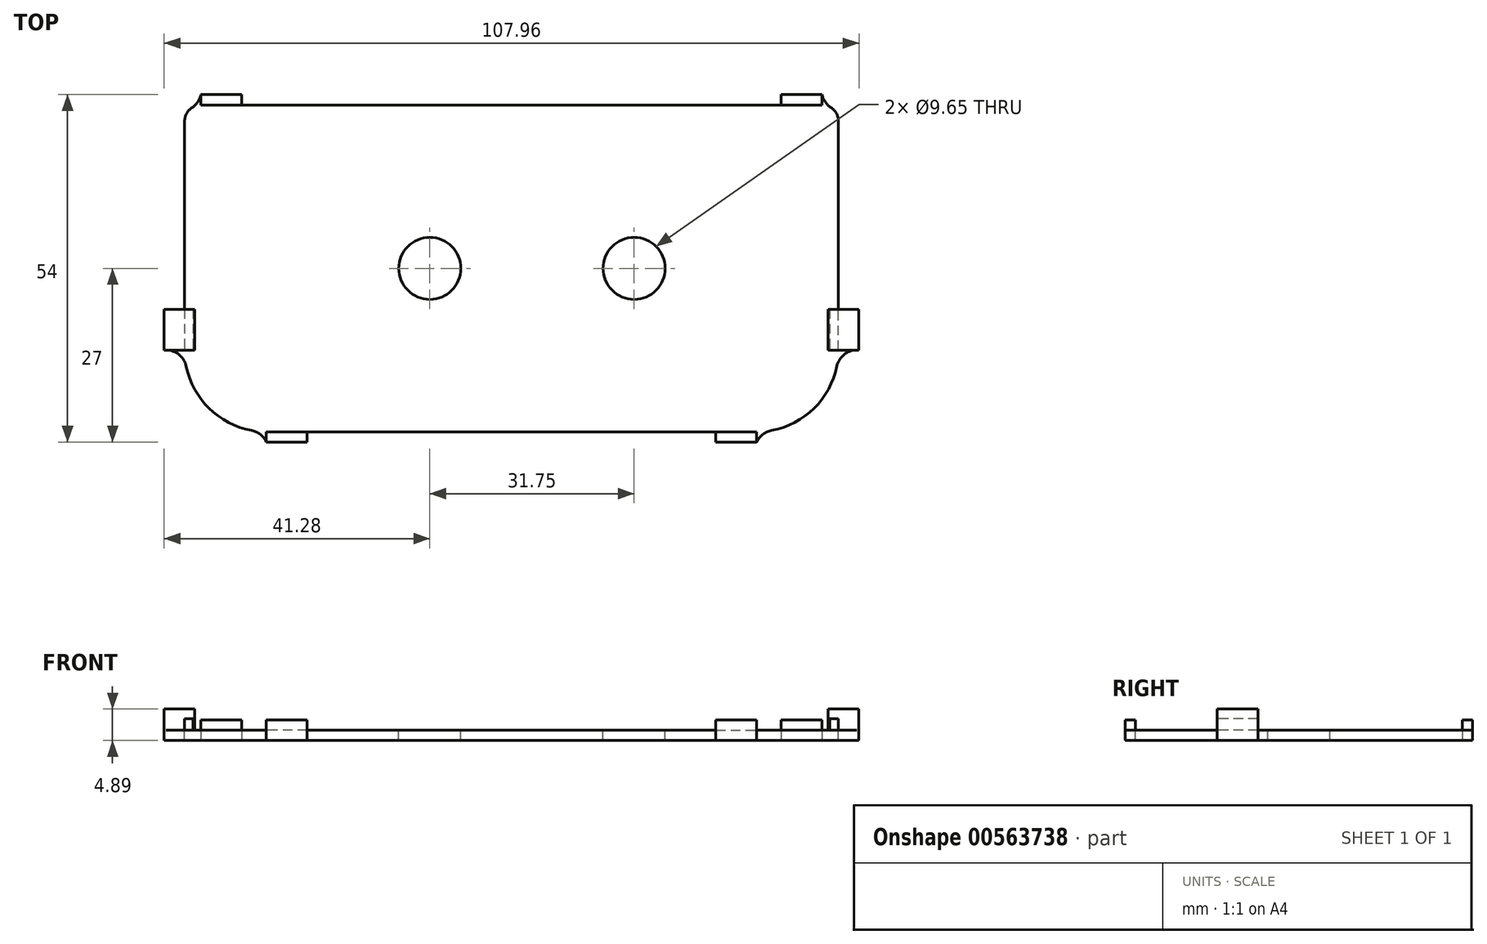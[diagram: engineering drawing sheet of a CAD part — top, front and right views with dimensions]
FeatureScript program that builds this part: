
annotation { "Feature Type Name" : "Feature", "Feature Type Description" : "" }
export const myFeature = defineFeature(function(context is Context, id is Id, definition is map)
    precondition{}
    {
        {
            var Q0;
            Q0=qCreatedBy(makeId("Top.planeOp"),FACE);
            var sketch = newSketch(context, id + "F0", { "sketchPlane" : qUnion([Q0])});
            skLineSegment(sketch, "E0.bottom", {"start": v(50.8, 25.4) * mm, "end": v(-50.8, 25.4) * mm});
            skLineSegment(sketch, "E0.top", {"start": v(50.8, -25.4) * mm, "end": v(-50.8, -25.4) * mm});
            skLineSegment(sketch, "E0.left", {"start": v(50.8, 25.4) * mm, "end": v(50.8, -25.4) * mm});
            skLineSegment(sketch, "E0.right", {"start": v(-50.8, 25.4) * mm, "end": v(-50.8, -25.4) * mm});
            skPoint(sketch, "E0.middle", {"position": v(0, 0) * mm});
            skLineSegment(sketch, "E1", {"start": v(-50.8, 0) * mm, "end": v(50.8, 0) * mm, "construction": true});
            skCircle(sketch, "E2", {"center": v(19.05, 0) * mm, "radius": 1.9 * mm});
            skCircle(sketch, "E3", {"center": v(-12.7, 0) * mm, "radius": 1.9 * mm});
            skSolve(sketch);
        }
        {
            var Q0;
            Q0=makeQuery(id+"F0.imprint","IMPRINT",FACE,{"disambiguationData":[TD([[makeQuery(id+"F0.imprint","IMPRINT",EDGE,{"derivedFrom":sQuery(id+"F0.wireOp",EDGE,"E0.bottom")}),1.0]])]});
            extrude(context, id + "F1", {"entities" : qUnion([Q0]), "depth" : 1.59 * mm, "offsetDistance" : 25.4 * mm});
        }
        {
            var Q0;
            Q0=makeQuery(id+"F1.opExtrude","CAP_FACE",FACE,{"disambiguationData":[OSD([sQuery(id+"F0.wireOp",EDGE,"E0.bottom"),sQuery(id+"F0.wireOp",EDGE,"E0.top"),sQuery(id+"F0.wireOp",EDGE,"E0.left"),sQuery(id+"F0.wireOp",EDGE,"E0.right"),sQuery(id+"F0.wireOp",EDGE,"E2"),sQuery(id+"F0.wireOp",EDGE,"E3")])],"isStart":false});
            var sketch = newSketch(context, id + "F2", { "sketchPlane" : qUnion([Q0])});
            skCircle(sketch, "E4", {"center": v(-12.7, 10.8) * mm, "radius": 3.18 * mm});
            skCircle(sketch, "E5", {"center": v(19.05, 10.8) * mm, "radius": 3.18 * mm});
            skLineSegment(sketch, "E6", {"start": v(-12.7, 10.8) * mm, "end": v(-12.7, -25.4) * mm, "construction": true});
            skLineSegment(sketch, "E7", {"start": v(19.05, 10.8) * mm, "end": v(19.05, -25.4) * mm, "construction": true});
            skCircle(sketch, "E8", {"center": v(19.05, -10.8) * mm, "radius": 3.18 * mm});
            skCircle(sketch, "E9", {"center": v(-12.7, -10.8) * mm, "radius": 3.18 * mm});
            skCircle(sketch, "E10", {"center": v(19.05, 0) * mm, "radius": 4.83 * mm});
            skCircle(sketch, "E11", {"center": v(-12.7, 0) * mm, "radius": 4.83 * mm});
            skSolve(sketch);
        }
        {
            var Q0;
            Q0=makeQuery(id+"F1.opExtrude","SWEPT_EDGE",EDGE,{"disambiguationData":[OSD([sQuery(id+"F0.wireOp",EDGE,"E0.top"),sQuery(id+"F0.wireOp",EDGE,"E0.right")])]});
            var Q1;
            Q1=makeQuery(id+"F1.opExtrude","SWEPT_EDGE",EDGE,{"disambiguationData":[OSD([sQuery(id+"F0.wireOp",EDGE,"E0.top"),sQuery(id+"F0.wireOp",EDGE,"E0.left")])]});
            fillet(context, id + "F3", {"entities" : qUnion([Q0, Q1]), "radius" : 12.7 * mm, "tangentPropagation" : true, "allowEdgeOverflow" : false});
        }
        {
            var Q0;
            Q0=makeQuery(id+"F1.opExtrude","SWEPT_EDGE",EDGE,{"disambiguationData":[OSD([sQuery(id+"F0.wireOp",EDGE,"E0.bottom"),sQuery(id+"F0.wireOp",EDGE,"E0.right")])]});
            var Q1;
            Q1=makeQuery(id+"F1.opExtrude","SWEPT_EDGE",EDGE,{"disambiguationData":[OSD([sQuery(id+"F0.wireOp",EDGE,"E0.bottom"),sQuery(id+"F0.wireOp",EDGE,"E0.left")])]});
            fillet(context, id + "F4", {"entities" : qUnion([Q0, Q1]), "radius" : 2.54 * mm, "tangentPropagation" : true, "allowEdgeOverflow" : false});
        }
        {
            var Q0;
            Q0=makeQuery(id+"F2.imprint","IMPRINT",FACE,{"disambiguationData":[TD([[makeQuery(id+"F2.imprint","IMPRINT",EDGE,{"derivedFrom":sQuery(id+"F2.wireOp",EDGE,"E11")}),1.0]])]});
            var Q1;
            Q1=makeQuery(id+"F2.imprint","IMPRINT",FACE,{"disambiguationData":[TD([[makeQuery(id+"F2.imprint","IMPRINT",EDGE,{"derivedFrom":sQuery(id+"F2.wireOp",EDGE,"E10")}),1.0]])]});
            extrude(context, id + "F5", {"entities" : qUnion([Q0, Q1]), "operationType" : NewBodyOperationType.REMOVE, "oppositeDirection" : true, "depth" : 3.17 * mm, "offsetDistance" : 25.4 * mm});
        }
        {
            var Q0;
            Q0=makeQuery(id+"F1.opExtrude","SWEPT_FACE",FACE,{"disambiguationData":[OSD([sQuery(id+"F0.wireOp",EDGE,"E0.bottom")])]});
            var sketch = newSketch(context, id + "F6", { "sketchPlane" : qUnion([Q0])});
            skLineSegment(sketch, "E12.bottom", {"start": v(-48.26, 1.59) * mm, "end": v(-41.91, 1.59) * mm});
            skLineSegment(sketch, "E12.top", {"start": v(-48.26, 0) * mm, "end": v(-41.91, 0) * mm});
            skLineSegment(sketch, "E12.left", {"start": v(-48.26, 1.59) * mm, "end": v(-48.26, 0) * mm});
            skLineSegment(sketch, "E12.right", {"start": v(-41.91, 1.59) * mm, "end": v(-41.91, 0) * mm});
            skLineSegment(sketch, "E13.bottom", {"start": v(48.26, 1.59) * mm, "end": v(41.91, 1.59) * mm});
            skLineSegment(sketch, "E13.top", {"start": v(48.26, 0) * mm, "end": v(41.91, 0) * mm});
            skLineSegment(sketch, "E13.left", {"start": v(48.26, 1.59) * mm, "end": v(48.26, 0) * mm});
            skLineSegment(sketch, "E13.right", {"start": v(41.91, 1.59) * mm, "end": v(41.91, 0) * mm});
            skSolve(sketch);
        }
        {
            var Q0;
            Q0=makeQuery(id+"F6.imprint","IMPRINT",FACE,{"disambiguationData":[TD([[makeQuery(id+"F6.imprint","IMPRINT",EDGE,{"derivedFrom":sQuery(id+"F6.wireOp",EDGE,"E12.bottom")}),-1.0]])]});
            var Q1;
            Q1=makeQuery(id+"F6.imprint","IMPRINT",FACE,{"disambiguationData":[TD([[makeQuery(id+"F6.imprint","IMPRINT",EDGE,{"derivedFrom":sQuery(id+"F6.wireOp",EDGE,"E13.bottom")}),-1.0]])]});
            extrude(context, id + "F7", {"entities" : qUnion([Q0, Q1]), "operationType" : NewBodyOperationType.ADD, "depth" : 1.6 * mm, "offsetDistance" : 25.4 * mm});
        }
        {
            var Q0;
            Q0=makeQuery(id+"F1.opExtrude","SWEPT_FACE",FACE,{"disambiguationData":[OSD([sQuery(id+"F0.wireOp",EDGE,"E0.top")])]});
            var sketch = newSketch(context, id + "F8", { "sketchPlane" : qUnion([Q0])});
            skLineSegment(sketch, "E14.bottom", {"start": v(-38.1, 0) * mm, "end": v(-31.75, 0) * mm});
            skLineSegment(sketch, "E14.top", {"start": v(-38.1, 1.59) * mm, "end": v(-31.75, 1.59) * mm});
            skLineSegment(sketch, "E14.left", {"start": v(-38.1, 0) * mm, "end": v(-38.1, 1.59) * mm});
            skLineSegment(sketch, "E14.right", {"start": v(-31.75, 0) * mm, "end": v(-31.75, 1.59) * mm});
            skLineSegment(sketch, "E15.bottom", {"start": v(38.1, 0) * mm, "end": v(31.75, 0) * mm});
            skLineSegment(sketch, "E15.top", {"start": v(38.1, 1.59) * mm, "end": v(31.75, 1.59) * mm});
            skLineSegment(sketch, "E15.left", {"start": v(38.1, 0) * mm, "end": v(38.1, 1.59) * mm});
            skLineSegment(sketch, "E15.right", {"start": v(31.75, 0) * mm, "end": v(31.75, 1.59) * mm});
            skSolve(sketch);
        }
        {
            var Q0;
            Q0=makeQuery(id+"F8.imprint","IMPRINT",FACE,{"disambiguationData":[TD([[makeQuery(id+"F8.imprint","IMPRINT",EDGE,{"derivedFrom":sQuery(id+"F8.wireOp",EDGE,"E15.bottom")}),-1.0]])]});
            var Q1;
            Q1=makeQuery(id+"F8.imprint","IMPRINT",FACE,{"disambiguationData":[TD([[makeQuery(id+"F8.imprint","IMPRINT",EDGE,{"derivedFrom":sQuery(id+"F8.wireOp",EDGE,"E14.bottom")}),-1.0]])]});
            extrude(context, id + "F9", {"entities" : qUnion([Q0, Q1]), "operationType" : NewBodyOperationType.ADD, "depth" : 1.6 * mm, "offsetDistance" : 25.4 * mm});
        }
        {
            var Q0;
            Q0=makeQuery(id+"F1.opExtrude","SWEPT_FACE",FACE,{"disambiguationData":[OSD([sQuery(id+"F0.wireOp",EDGE,"E0.right")])]});
            var sketch = newSketch(context, id + "F10", { "sketchPlane" : qUnion([Q0])});
            skLineSegment(sketch, "E16.bottom", {"start": v(12.7, 0) * mm, "end": v(6.35, 0) * mm});
            skLineSegment(sketch, "E16.top", {"start": v(12.7, 1.59) * mm, "end": v(6.35, 1.59) * mm});
            skLineSegment(sketch, "E16.left", {"start": v(12.7, 0) * mm, "end": v(12.7, 1.59) * mm});
            skLineSegment(sketch, "E16.right", {"start": v(6.35, 0) * mm, "end": v(6.35, 1.59) * mm});
            skSolve(sketch);
        }
        {
            var Q0;
            Q0=makeQuery(id+"F10.imprint","IMPRINT",FACE,{"disambiguationData":[TD([[makeQuery(id+"F10.imprint","IMPRINT",EDGE,{"derivedFrom":sQuery(id+"F10.wireOp",EDGE,"E16.bottom")}),1.0]])]});
            extrude(context, id + "F11", {"entities" : qUnion([Q0]), "operationType" : NewBodyOperationType.ADD, "depth" : 3.17 * mm, "offsetDistance" : 25.4 * mm});
        }
        {
            var Q0;
            Q0=makeQuery(id+"F1.opExtrude","SWEPT_FACE",FACE,{"disambiguationData":[OSD([sQuery(id+"F0.wireOp",EDGE,"E0.left")])]});
            var sketch = newSketch(context, id + "F12", { "sketchPlane" : qUnion([Q0])});
            skLineSegment(sketch, "E17.bottom", {"start": v(-12.7, 0) * mm, "end": v(-6.35, 0) * mm});
            skLineSegment(sketch, "E17.top", {"start": v(-12.7, 1.59) * mm, "end": v(-6.35, 1.59) * mm});
            skLineSegment(sketch, "E17.left", {"start": v(-12.7, 0) * mm, "end": v(-12.7, 1.59) * mm});
            skLineSegment(sketch, "E17.right", {"start": v(-6.35, 0) * mm, "end": v(-6.35, 1.59) * mm});
            skSolve(sketch);
        }
        {
            var Q0;
            Q0=makeQuery(id+"F12.imprint","IMPRINT",FACE,{"disambiguationData":[TD([[makeQuery(id+"F12.imprint","IMPRINT",EDGE,{"derivedFrom":sQuery(id+"F12.wireOp",EDGE,"E17.bottom")}),-1.0]])]});
            extrude(context, id + "F13", {"entities" : qUnion([Q0]), "operationType" : NewBodyOperationType.ADD, "depth" : 3.17 * mm, "offsetDistance" : 25.4 * mm});
        }
        {
            var Q0;
            Q0=makeQuery(id+"F13.boolean.opBoolean","MERGE",FACE,{"derivedFrom":[makeQuery(id+"F11.boolean.opBoolean","MERGE",FACE,{"derivedFrom":[makeQuery(id+"F9.boolean.opBoolean","MERGE",FACE,{"derivedFrom":[makeQuery(id+"F7.boolean.opBoolean","MERGE",FACE,{"derivedFrom":[makeQuery(id+"F1.opExtrude","CAP_FACE",FACE,{"disambiguationData":[OSD([sQuery(id+"F0.wireOp",EDGE,"E0.bottom"),sQuery(id+"F0.wireOp",EDGE,"E0.top"),sQuery(id+"F0.wireOp",EDGE,"E0.left"),sQuery(id+"F0.wireOp",EDGE,"E0.right"),sQuery(id+"F0.wireOp",EDGE,"E2"),sQuery(id+"F0.wireOp",EDGE,"E3")])],"isStart":false}),makeQuery(id+"F7.opExtrude","SWEPT_FACE",FACE,{"disambiguationData":[OSD([sQuery(id+"F6.wireOp",EDGE,"E12.bottom")])]}),makeQuery(id+"F7.opExtrude","SWEPT_FACE",FACE,{"disambiguationData":[OSD([sQuery(id+"F6.wireOp",EDGE,"E13.bottom")])]})]}),makeQuery(id+"F9.opExtrude","SWEPT_FACE",FACE,{"disambiguationData":[OSD([sQuery(id+"F8.wireOp",EDGE,"E14.top")])]}),makeQuery(id+"F9.opExtrude","SWEPT_FACE",FACE,{"disambiguationData":[OSD([sQuery(id+"F8.wireOp",EDGE,"E15.top")])]})]}),makeQuery(id+"F11.opExtrude","SWEPT_FACE",FACE,{"disambiguationData":[OSD([sQuery(id+"F10.wireOp",EDGE,"E16.top")])]})]}),makeQuery(id+"F13.opExtrude","SWEPT_FACE",FACE,{"disambiguationData":[OSD([sQuery(id+"F12.wireOp",EDGE,"E17.top")])]})]});
            var sketch = newSketch(context, id + "F14", { "sketchPlane" : qUnion([Q0])});
            skLineSegment(sketch, "E18.bottom", {"start": v(31.75, -27) * mm, "end": v(38.1, -27) * mm});
            skLineSegment(sketch, "E18.top", {"start": v(31.75, -25.4) * mm, "end": v(38.1, -25.4) * mm});
            skLineSegment(sketch, "E18.left", {"start": v(31.75, -27) * mm, "end": v(31.75, -25.4) * mm});
            skLineSegment(sketch, "E18.right", {"start": v(38.1, -27) * mm, "end": v(38.1, -25.4) * mm});
            skLineSegment(sketch, "E19.bottom", {"start": v(53.98, -12.7) * mm, "end": v(50.8, -12.7) * mm});
            skLineSegment(sketch, "E19.top", {"start": v(53.98, -6.35) * mm, "end": v(50.8, -6.35) * mm});
            skLineSegment(sketch, "E19.left", {"start": v(53.98, -12.7) * mm, "end": v(53.98, -6.35) * mm});
            skLineSegment(sketch, "E19.right", {"start": v(50.8, -12.7) * mm, "end": v(50.8, -6.35) * mm});
            skLineSegment(sketch, "E20.bottom", {"start": v(48.26, 27) * mm, "end": v(41.91, 27) * mm});
            skLineSegment(sketch, "E20.top", {"start": v(48.26, 25.4) * mm, "end": v(41.91, 25.4) * mm});
            skLineSegment(sketch, "E20.left", {"start": v(48.26, 27) * mm, "end": v(48.26, 25.4) * mm});
            skLineSegment(sketch, "E20.right", {"start": v(41.91, 27) * mm, "end": v(41.91, 25.4) * mm});
            skLineSegment(sketch, "E21.bottom", {"start": v(-41.91, 27) * mm, "end": v(-48.26, 27) * mm});
            skLineSegment(sketch, "E21.top", {"start": v(-41.91, 25.4) * mm, "end": v(-48.26, 25.4) * mm});
            skLineSegment(sketch, "E21.left", {"start": v(-41.91, 27) * mm, "end": v(-41.91, 25.4) * mm});
            skLineSegment(sketch, "E21.right", {"start": v(-48.26, 27) * mm, "end": v(-48.26, 25.4) * mm});
            skLineSegment(sketch, "E22.bottom", {"start": v(-53.98, -12.7) * mm, "end": v(-50.8, -12.7) * mm});
            skLineSegment(sketch, "E22.top", {"start": v(-53.98, -6.35) * mm, "end": v(-50.8, -6.35) * mm});
            skLineSegment(sketch, "E22.left", {"start": v(-53.98, -12.7) * mm, "end": v(-53.98, -6.35) * mm});
            skLineSegment(sketch, "E22.right", {"start": v(-50.8, -12.7) * mm, "end": v(-50.8, -6.35) * mm});
            skLineSegment(sketch, "E23.bottom", {"start": v(-31.75, -25.4) * mm, "end": v(-38.1, -25.4) * mm});
            skLineSegment(sketch, "E23.top", {"start": v(-31.75, -27) * mm, "end": v(-38.1, -27) * mm});
            skLineSegment(sketch, "E23.left", {"start": v(-31.75, -25.4) * mm, "end": v(-31.75, -27) * mm});
            skLineSegment(sketch, "E23.right", {"start": v(-38.1, -25.4) * mm, "end": v(-38.1, -27) * mm});
            skSolve(sketch);
        }
        {
            var Q0;
            Q0=makeQuery(id+"F14.imprint","IMPRINT",FACE,{"disambiguationData":[TD([[makeQuery(id+"F14.imprint","IMPRINT",EDGE,{"derivedFrom":sQuery(id+"F14.wireOp",EDGE,"E20.bottom")}),1.0]])]});
            var Q1;
            Q1=makeQuery(id+"F14.imprint","IMPRINT",FACE,{"disambiguationData":[TD([[makeQuery(id+"F14.imprint","IMPRINT",EDGE,{"derivedFrom":sQuery(id+"F14.wireOp",EDGE,"E18.bottom")}),-1.0]])]});
            var Q2;
            Q2=makeQuery(id+"F14.imprint","IMPRINT",FACE,{"disambiguationData":[TD([[makeQuery(id+"F14.imprint","IMPRINT",EDGE,{"derivedFrom":sQuery(id+"F14.wireOp",EDGE,"E23.bottom")}),1.0]])]});
            var Q3;
            Q3=makeQuery(id+"F14.imprint","IMPRINT",FACE,{"disambiguationData":[TD([[makeQuery(id+"F14.imprint","IMPRINT",EDGE,{"derivedFrom":sQuery(id+"F14.wireOp",EDGE,"E21.bottom")}),1.0]])]});
            extrude(context, id + "F15", {"entities" : qUnion([Q0, Q1, Q2, Q3]), "operationType" : NewBodyOperationType.ADD, "depth" : 1.59 * mm, "offsetDistance" : 25.4 * mm});
        }
        {
            var Q0;
            Q0=makeQuery(id+"F14.imprint","IMPRINT",FACE,{"disambiguationData":[TD([[makeQuery(id+"F14.imprint","IMPRINT",EDGE,{"derivedFrom":sQuery(id+"F14.wireOp",EDGE,"E19.bottom")}),-1.0]])]});
            var Q1;
            Q1=makeQuery(id+"F14.imprint","IMPRINT",FACE,{"disambiguationData":[TD([[makeQuery(id+"F14.imprint","IMPRINT",EDGE,{"derivedFrom":sQuery(id+"F14.wireOp",EDGE,"E22.bottom")}),1.0]])]});
            extrude(context, id + "F16", {"entities" : qUnion([Q0, Q1]), "operationType" : NewBodyOperationType.ADD, "depth" : 3.3 * mm, "offsetDistance" : 25.4 * mm});
        }
        {
            var Q0;
            Q0=makeQuery(id+"F16.opExtrude","SWEPT_FACE",FACE,{"disambiguationData":[OSD([sQuery(id+"F14.wireOp",EDGE,"E22.right")])]});
            var sketch = newSketch(context, id + "F17", { "sketchPlane" : qUnion([Q0])});
            skLineSegment(sketch, "E24.bottom", {"start": v(-6.35, 4.89) * mm, "end": v(-12.7, 4.89) * mm});
            skLineSegment(sketch, "E24.top", {"start": v(-6.35, 3.37) * mm, "end": v(-12.7, 3.37) * mm});
            skLineSegment(sketch, "E24.left", {"start": v(-6.35, 4.89) * mm, "end": v(-6.35, 3.37) * mm});
            skLineSegment(sketch, "E24.right", {"start": v(-12.7, 4.89) * mm, "end": v(-12.7, 3.37) * mm});
            skSolve(sketch);
        }
        {
            var Q0;
            Q0=makeQuery(id+"F17.imprint","IMPRINT",FACE,{"disambiguationData":[TD([[makeQuery(id+"F17.imprint","IMPRINT",EDGE,{"derivedFrom":sQuery(id+"F17.wireOp",EDGE,"E24.bottom")}),-1.0]])]});
            extrude(context, id + "F18", {"entities" : qUnion([Q0]), "operationType" : NewBodyOperationType.ADD, "depth" : 1.59 * mm, "offsetDistance" : 25.4 * mm});
        }
        {
            var Q0;
            Q0=makeQuery(id+"F16.opExtrude","SWEPT_FACE",FACE,{"disambiguationData":[OSD([sQuery(id+"F14.wireOp",EDGE,"E19.right")])]});
            var sketch = newSketch(context, id + "F19", { "sketchPlane" : qUnion([Q0])});
            skLineSegment(sketch, "E25.bottom", {"start": v(12.7, 4.89) * mm, "end": v(6.35, 4.89) * mm});
            skLineSegment(sketch, "E25.top", {"start": v(12.7, 3.37) * mm, "end": v(6.35, 3.37) * mm});
            skLineSegment(sketch, "E25.left", {"start": v(12.7, 4.89) * mm, "end": v(12.7, 3.37) * mm});
            skLineSegment(sketch, "E25.right", {"start": v(6.35, 4.89) * mm, "end": v(6.35, 3.37) * mm});
            skSolve(sketch);
        }
        {
            var Q0;
            Q0=makeQuery(id+"F19.imprint","IMPRINT",FACE,{"disambiguationData":[TD([[makeQuery(id+"F19.imprint","IMPRINT",EDGE,{"derivedFrom":sQuery(id+"F19.wireOp",EDGE,"E25.bottom")}),1.0]])]});
            extrude(context, id + "F20", {"entities" : qUnion([Q0]), "operationType" : NewBodyOperationType.ADD, "depth" : 1.59 * mm, "offsetDistance" : 25.4 * mm});
        }
        {
            var Q0;
            Q0=makeQuery(id+"F9.opExtrude","CAP_EDGE",EDGE,{"disambiguationData":[OSD([sQuery(id+"F8.wireOp",EDGE,"E14.right")])],"isStart":true});
            var Q1;
            {var subQ0=sQuery(id+"F0.wireOp",EDGE,"E0.top");Q1=makeQuery(id+"F9.boolean.opBoolean","MERGE",EDGE,{"derivedFrom":[makeQuery(id+"F3.opFillet","BLEND_EDGE",EDGE,{"blendedFrom":[makeQuery(id+"F1.opExtrude","SWEPT_EDGE",EDGE,{"disambiguationData":[OSD([subQ0,sQuery(id+"F0.wireOp",EDGE,"E0.right")])]}),makeQuery(id+"F1.opExtrude","SWEPT_FACE",FACE,{"disambiguationData":[OSD([subQ0])]})],"blendedInto":[makeQuery(id+"F1.opExtrude","SWEPT_FACE",FACE,{"disambiguationData":[OSD([subQ0])]})]}),makeQuery(id+"F9.opExtrude","CAP_EDGE",EDGE,{"disambiguationData":[OSD([sQuery(id+"F8.wireOp",EDGE,"E14.left")])],"isStart":true})]});}
            var Q2;
            {var subQ0=sQuery(id+"F0.wireOp",EDGE,"E0.right");Q2=makeQuery(id+"F11.boolean.opBoolean","MERGE",EDGE,{"derivedFrom":[makeQuery(id+"F3.opFillet","BLEND_EDGE",EDGE,{"blendedFrom":[makeQuery(id+"F1.opExtrude","SWEPT_EDGE",EDGE,{"disambiguationData":[OSD([sQuery(id+"F0.wireOp",EDGE,"E0.top"),subQ0])]}),makeQuery(id+"F1.opExtrude","SWEPT_FACE",FACE,{"disambiguationData":[OSD([subQ0])]})],"blendedInto":[makeQuery(id+"F1.opExtrude","SWEPT_FACE",FACE,{"disambiguationData":[OSD([subQ0])]})]}),makeQuery(id+"F11.opExtrude","CAP_EDGE",EDGE,{"disambiguationData":[OSD([sQuery(id+"F10.wireOp",EDGE,"E16.left")])],"isStart":true})]});}
            var Q3;
            Q3=makeQuery(id+"F11.opExtrude","CAP_EDGE",EDGE,{"disambiguationData":[OSD([sQuery(id+"F10.wireOp",EDGE,"E16.right")])],"isStart":true});
            var Q4;
            {var subQ0=sQuery(id+"F0.wireOp",EDGE,"E0.bottom");Q4=makeQuery(id+"F7.boolean.opBoolean","MERGE",EDGE,{"derivedFrom":[makeQuery(id+"F4.opFillet","BLEND_EDGE",EDGE,{"blendedFrom":[makeQuery(id+"F1.opExtrude","SWEPT_EDGE",EDGE,{"disambiguationData":[OSD([subQ0,sQuery(id+"F0.wireOp",EDGE,"E0.right")])]}),makeQuery(id+"F1.opExtrude","SWEPT_FACE",FACE,{"disambiguationData":[OSD([subQ0])]})],"blendedInto":[makeQuery(id+"F1.opExtrude","SWEPT_FACE",FACE,{"disambiguationData":[OSD([subQ0])]})]}),makeQuery(id+"F7.opExtrude","CAP_EDGE",EDGE,{"disambiguationData":[OSD([sQuery(id+"F6.wireOp",EDGE,"E13.left")])],"isStart":true})]});}
            var Q5;
            Q5=makeQuery(id+"F7.opExtrude","CAP_EDGE",EDGE,{"disambiguationData":[OSD([sQuery(id+"F6.wireOp",EDGE,"E13.right")])],"isStart":true});
            var Q6;
            {var subQ0=sQuery(id+"F0.wireOp",EDGE,"E0.bottom");Q6=makeQuery(id+"F7.boolean.opBoolean","MERGE",EDGE,{"derivedFrom":[makeQuery(id+"F4.opFillet","BLEND_EDGE",EDGE,{"blendedFrom":[makeQuery(id+"F1.opExtrude","SWEPT_EDGE",EDGE,{"disambiguationData":[OSD([subQ0,sQuery(id+"F0.wireOp",EDGE,"E0.left")])]}),makeQuery(id+"F1.opExtrude","SWEPT_FACE",FACE,{"disambiguationData":[OSD([subQ0])]})],"blendedInto":[makeQuery(id+"F1.opExtrude","SWEPT_FACE",FACE,{"disambiguationData":[OSD([subQ0])]})]}),makeQuery(id+"F7.opExtrude","CAP_EDGE",EDGE,{"disambiguationData":[OSD([sQuery(id+"F6.wireOp",EDGE,"E12.left")])],"isStart":true})]});}
            var Q7;
            Q7=makeQuery(id+"F7.opExtrude","CAP_EDGE",EDGE,{"disambiguationData":[OSD([sQuery(id+"F6.wireOp",EDGE,"E12.right")])],"isStart":true});
            var Q8;
            Q8=makeQuery(id+"F13.opExtrude","CAP_EDGE",EDGE,{"disambiguationData":[OSD([sQuery(id+"F12.wireOp",EDGE,"E17.right")])],"isStart":true});
            var Q9;
            {var subQ0=sQuery(id+"F0.wireOp",EDGE,"E0.left");Q9=makeQuery(id+"F13.boolean.opBoolean","MERGE",EDGE,{"derivedFrom":[makeQuery(id+"F3.opFillet","BLEND_EDGE",EDGE,{"blendedFrom":[makeQuery(id+"F1.opExtrude","SWEPT_EDGE",EDGE,{"disambiguationData":[OSD([sQuery(id+"F0.wireOp",EDGE,"E0.top"),subQ0])]}),makeQuery(id+"F1.opExtrude","SWEPT_FACE",FACE,{"disambiguationData":[OSD([subQ0])]})],"blendedInto":[makeQuery(id+"F1.opExtrude","SWEPT_FACE",FACE,{"disambiguationData":[OSD([subQ0])]})]}),makeQuery(id+"F13.opExtrude","CAP_EDGE",EDGE,{"disambiguationData":[OSD([sQuery(id+"F12.wireOp",EDGE,"E17.left")])],"isStart":true})]});}
            var Q10;
            {var subQ0=sQuery(id+"F0.wireOp",EDGE,"E0.top");Q10=makeQuery(id+"F9.boolean.opBoolean","MERGE",EDGE,{"derivedFrom":[makeQuery(id+"F3.opFillet","BLEND_EDGE",EDGE,{"blendedFrom":[makeQuery(id+"F1.opExtrude","SWEPT_EDGE",EDGE,{"disambiguationData":[OSD([subQ0,sQuery(id+"F0.wireOp",EDGE,"E0.left")])]}),makeQuery(id+"F1.opExtrude","SWEPT_FACE",FACE,{"disambiguationData":[OSD([subQ0])]})],"blendedInto":[makeQuery(id+"F1.opExtrude","SWEPT_FACE",FACE,{"disambiguationData":[OSD([subQ0])]})]}),makeQuery(id+"F9.opExtrude","CAP_EDGE",EDGE,{"disambiguationData":[OSD([sQuery(id+"F8.wireOp",EDGE,"E15.left")])],"isStart":true})]});}
            var Q11;
            Q11=makeQuery(id+"F9.opExtrude","CAP_EDGE",EDGE,{"disambiguationData":[OSD([sQuery(id+"F8.wireOp",EDGE,"E15.right")])],"isStart":true});
            fillet(context, id + "F21", {"entities" : qUnion([Q0, Q1, Q2, Q3, Q4, Q5, Q6, Q7, Q8, Q9, Q10, Q11]), "radius" : 3.17 * mm, "tangentPropagation" : true, "allowEdgeOverflow" : false});
        }
        {
            var Q0;
            Q0=makeQuery(id+"F20.opExtrude","SWEPT_FACE",FACE,{"disambiguationData":[OSD([sQuery(id+"F19.wireOp",EDGE,"E25.top")])]});
            var sketch = newSketch(context, id + "F22", { "sketchPlane" : qUnion([Q0])});
            skLineSegment(sketch, "E26.bottom", {"start": v(49.21, 6.35) * mm, "end": v(49.47, 6.35) * mm});
            skLineSegment(sketch, "E26.top", {"start": v(49.21, 12.7) * mm, "end": v(49.47, 12.7) * mm});
            skLineSegment(sketch, "E26.left", {"start": v(49.21, 6.35) * mm, "end": v(49.21, 12.7) * mm});
            skLineSegment(sketch, "E26.right", {"start": v(49.47, 6.35) * mm, "end": v(49.47, 12.7) * mm});
            skSolve(sketch);
        }
        {
            var Q0;
            Q0=makeQuery(id+"F22.imprint","IMPRINT",FACE,{"disambiguationData":[TD([[makeQuery(id+"F22.imprint","IMPRINT",EDGE,{"derivedFrom":sQuery(id+"F22.wireOp",EDGE,"E26.bottom")}),1.0]])]});
            extrude(context, id + "F23", {"entities" : qUnion([Q0]), "operationType" : NewBodyOperationType.ADD, "depth" : 2.03 * mm, "offsetDistance" : 25.4 * mm});
        }
        {
            var Q0;
            Q0=makeQuery(id+"F18.opExtrude","SWEPT_FACE",FACE,{"disambiguationData":[OSD([sQuery(id+"F17.wireOp",EDGE,"E24.top")])]});
            var sketch = newSketch(context, id + "F24", { "sketchPlane" : qUnion([Q0])});
            skLineSegment(sketch, "E27.bottom", {"start": v(-49.21, 6.35) * mm, "end": v(-49.47, 6.35) * mm});
            skLineSegment(sketch, "E27.top", {"start": v(-49.21, 12.7) * mm, "end": v(-49.47, 12.7) * mm});
            skLineSegment(sketch, "E27.left", {"start": v(-49.21, 6.35) * mm, "end": v(-49.21, 12.7) * mm});
            skLineSegment(sketch, "E27.right", {"start": v(-49.47, 6.35) * mm, "end": v(-49.47, 12.7) * mm});
            skSolve(sketch);
        }
        {
            var Q0;
            Q0=makeQuery(id+"F24.imprint","IMPRINT",FACE,{"disambiguationData":[TD([[makeQuery(id+"F24.imprint","IMPRINT",EDGE,{"derivedFrom":sQuery(id+"F24.wireOp",EDGE,"E27.bottom")}),-1.0]])]});
            extrude(context, id + "F25", {"entities" : qUnion([Q0]), "operationType" : NewBodyOperationType.ADD, "depth" : 2.03 * mm, "offsetDistance" : 25.4 * mm});
        }
    });
